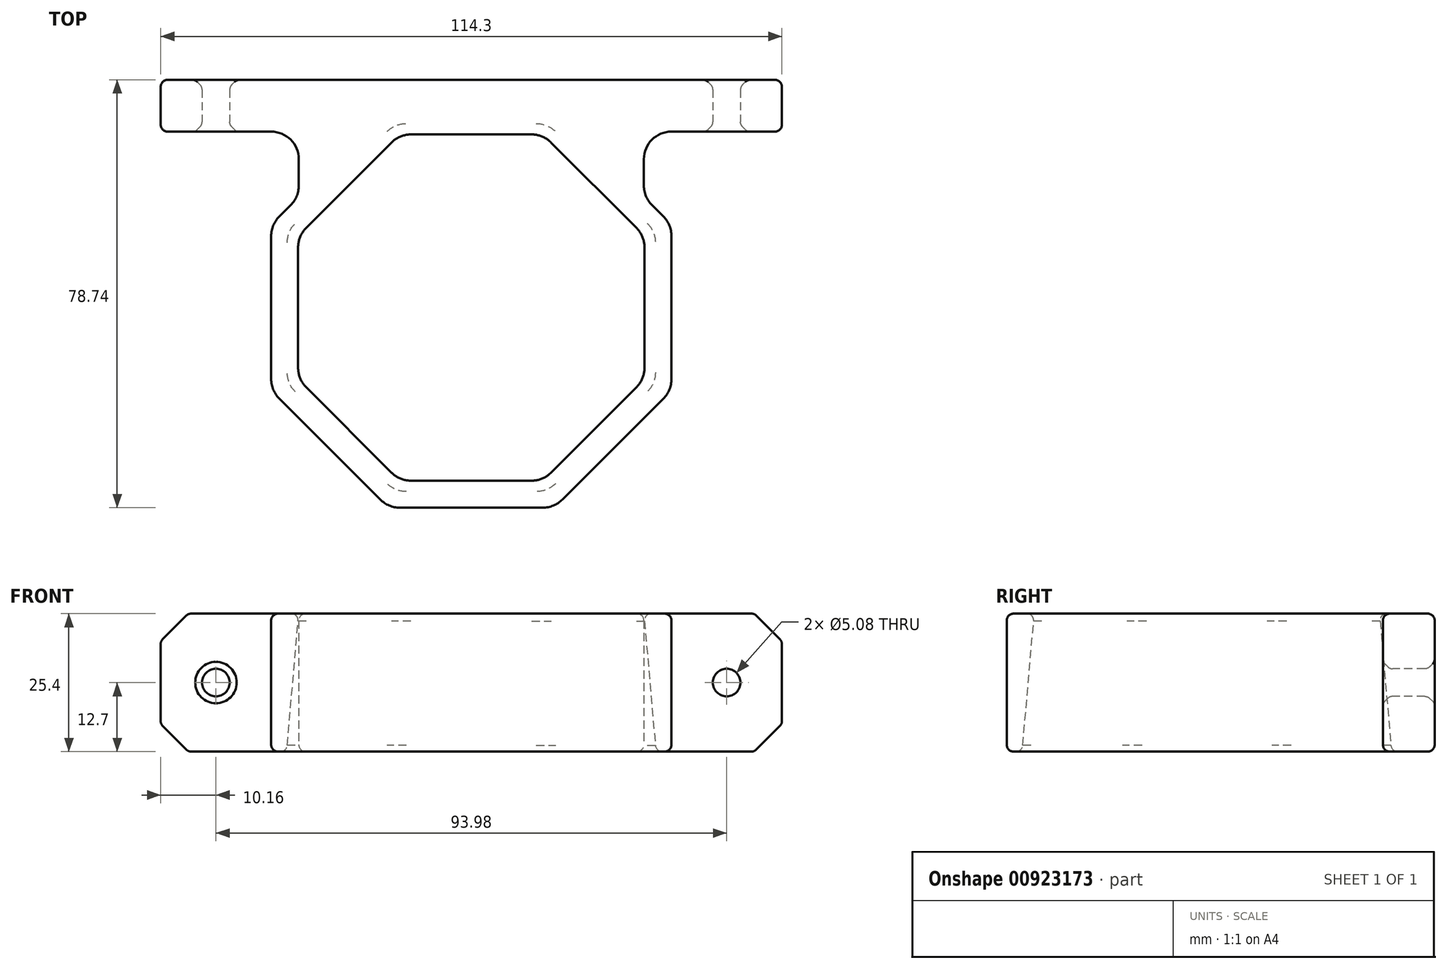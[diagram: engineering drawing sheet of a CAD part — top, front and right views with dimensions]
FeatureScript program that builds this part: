
annotation { "Feature Type Name" : "Feature", "Feature Type Description" : "" }
export const myFeature = defineFeature(function(context is Context, id is Id, definition is map)
    precondition{}
    {
        {
            var Q0;
            Q0=qCreatedBy(makeId("Top.planeOp"),FACE);
            var sketch = newSketch(context, id + "F0", { "sketchPlane" : qUnion([Q0])});
            skCircle(sketch, "E0.cCircle", {"center": v(0, 0) * mm, "radius": 31.75 * mm, "construction": true});
            skLineSegment(sketch, "E0.0", {"start": v(31.75, 13.15) * mm, "end": v(31.75, -13.15) * mm});
            skLineSegment(sketch, "E0.1", {"start": v(31.75, -13.15) * mm, "end": v(13.15, -31.75) * mm});
            skLineSegment(sketch, "E0.2", {"start": v(13.15, -31.75) * mm, "end": v(-13.15, -31.75) * mm});
            skLineSegment(sketch, "E0.3", {"start": v(-13.15, -31.75) * mm, "end": v(-31.75, -13.15) * mm});
            skLineSegment(sketch, "E0.4", {"start": v(-31.75, -13.15) * mm, "end": v(-31.75, 13.15) * mm});
            skLineSegment(sketch, "E0.5", {"start": v(-31.75, 13.15) * mm, "end": v(-13.15, 31.75) * mm});
            skLineSegment(sketch, "E0.6", {"start": v(-13.15, 31.75) * mm, "end": v(13.15, 31.75) * mm});
            skLineSegment(sketch, "E0.7", {"start": v(13.15, 31.75) * mm, "end": v(31.75, 13.15) * mm});
            skPoint(sketch, "E0.0.midPoint", {"position": v(31.75, 0) * mm});
            skLineSegment(sketch, "E1.0", {"start": v(-15.26, 36.83) * mm, "end": v(15.26, 36.83) * mm});
            skLineSegment(sketch, "E1.1", {"start": v(-36.83, 15.26) * mm, "end": v(-15.26, 36.83) * mm});
            skLineSegment(sketch, "E1.2", {"start": v(15.26, 36.83) * mm, "end": v(36.83, 15.26) * mm});
            skLineSegment(sketch, "E1.3", {"start": v(-36.83, -15.26) * mm, "end": v(-36.83, 15.26) * mm});
            skLineSegment(sketch, "E1.4", {"start": v(36.83, 15.26) * mm, "end": v(36.83, -15.26) * mm});
            skLineSegment(sketch, "E1.5", {"start": v(36.83, -15.26) * mm, "end": v(15.26, -36.83) * mm});
            skLineSegment(sketch, "E1.6", {"start": v(15.26, -36.83) * mm, "end": v(-15.26, -36.83) * mm});
            skLineSegment(sketch, "E1.7", {"start": v(-15.26, -36.83) * mm, "end": v(-36.83, -15.26) * mm});
            skLineSegment(sketch, "E2", {"start": v(-31.75, 20.34) * mm, "end": v(-31.75, 41.91) * mm});
            skLineSegment(sketch, "E3", {"start": v(-31.75, 41.91) * mm, "end": v(31.75, 41.91) * mm});
            skLineSegment(sketch, "E4", {"start": v(31.75, 41.91) * mm, "end": v(31.75, 20.34) * mm});
            skLineSegment(sketch, "E5", {"start": v(-31.75, 41.91) * mm, "end": v(-57.15, 41.91) * mm});
            skLineSegment(sketch, "E6", {"start": v(-57.15, 41.91) * mm, "end": v(-57.15, 32.38) * mm});
            skLineSegment(sketch, "E7", {"start": v(-57.15, 32.38) * mm, "end": v(-31.75, 32.38) * mm});
            skLineSegment(sketch, "E8", {"start": v(31.75, 41.91) * mm, "end": v(57.15, 41.91) * mm});
            skLineSegment(sketch, "E9", {"start": v(57.15, 41.91) * mm, "end": v(57.15, 32.39) * mm});
            skLineSegment(sketch, "E10", {"start": v(57.15, 32.39) * mm, "end": v(31.75, 32.39) * mm});
            skSolve(sketch);
        }
        {
            var Q0;
            Q0 = qSketchRegion(id + "F0", true);
            extrude(context, id + "F1", {"entities" : qUnion([Q0]), "depth" : 25.4 * mm, "offsetDistance" : 25.4 * mm});
        }
        {
            var Q0;
            Q0=makeQuery(id+"F1.opExtrude","SWEPT_FACE",FACE,{"disambiguationData":[OSD([sQuery(id+"F0.wireOp",EDGE,"E7")])]});
            var sketch = newSketch(context, id + "F2", { "sketchPlane" : qUnion([Q0])});
            skLineSegment(sketch, "E11", {"start": v(-57.15, 12.7) * mm, "end": v(-46.99, 12.7) * mm, "construction": true});
            skLineSegment(sketch, "E12", {"start": v(47, 12.7) * mm, "end": v(57.15, 12.7) * mm, "construction": true});
            skCircle(sketch, "E13", {"center": v(-46.99, 12.7) * mm, "radius": 2.54 * mm});
            skCircle(sketch, "E14", {"center": v(47, 12.7) * mm, "radius": 2.54 * mm});
            skSolve(sketch);
        }
        {
            var Q0;
            Q0 = qSketchRegion(id + "F2", true);
            extrude(context, id + "F3", {"entities" : qUnion([Q0]), "operationType" : NewBodyOperationType.REMOVE, "endBound" : BoundingType.THROUGH_ALL, "oppositeDirection" : true, "depth" : 25.4 * mm, "offsetDistance" : 25.4 * mm});
        }
        {
            var Q0;
            Q0=makeQuery(id+"F1.opExtrude","CAP_EDGE",EDGE,{"disambiguationData":[OSD([sQuery(id+"F0.wireOp",EDGE,"E0.3")])],"isStart":true});
            var Q1;
            Q1=makeQuery(id+"F1.opExtrude","CAP_EDGE",EDGE,{"disambiguationData":[OSD([sQuery(id+"F0.wireOp",EDGE,"E0.2")])],"isStart":true});
            var Q2;
            Q2=makeQuery(id+"F1.opExtrude","CAP_EDGE",EDGE,{"disambiguationData":[OSD([sQuery(id+"F0.wireOp",EDGE,"E0.1")])],"isStart":true});
            var Q3;
            Q3=makeQuery(id+"F1.opExtrude","CAP_EDGE",EDGE,{"disambiguationData":[OSD([sQuery(id+"F0.wireOp",EDGE,"E0.0")])],"isStart":true});
            var Q4;
            Q4=makeQuery(id+"F1.opExtrude","CAP_EDGE",EDGE,{"disambiguationData":[OSD([sQuery(id+"F0.wireOp",EDGE,"E0.7")])],"isStart":true});
            var Q5;
            Q5=makeQuery(id+"F1.opExtrude","CAP_EDGE",EDGE,{"disambiguationData":[OSD([sQuery(id+"F0.wireOp",EDGE,"E0.6")])],"isStart":true});
            var Q6;
            Q6=makeQuery(id+"F1.opExtrude","CAP_EDGE",EDGE,{"disambiguationData":[OSD([sQuery(id+"F0.wireOp",EDGE,"E0.5")])],"isStart":true});
            var Q7;
            Q7=makeQuery(id+"F1.opExtrude","CAP_EDGE",EDGE,{"disambiguationData":[OSD([sQuery(id+"F0.wireOp",EDGE,"E0.4")])],"isStart":true});
            chamfer(context, id + "F4", {"entities" : qUnion([Q0, Q1, Q2, Q3, Q4, Q5, Q6, Q7]), "chamferType" : ChamferType.OFFSET_ANGLE, "width" : 25.4 * mm, "oppositeDirection" : false, "angle" : 5 * degree, "tangentPropagation" : true});
        }
        {
            var Q0;
            Q0=makeQuery(id+"F1.opExtrude","SWEPT_EDGE",EDGE,{"disambiguationData":[OSD([sQuery(id+"F0.wireOp",EDGE,"E1.6"),sQuery(id+"F0.wireOp",EDGE,"E1.7")])]});
            var Q1;
            Q1=makeQuery(id+"F1.opExtrude","SWEPT_EDGE",EDGE,{"disambiguationData":[OSD([sQuery(id+"F0.wireOp",EDGE,"E1.5"),sQuery(id+"F0.wireOp",EDGE,"E1.6")])]});
            var Q2;
            Q2=makeQuery(id+"F1.opExtrude","SWEPT_EDGE",EDGE,{"disambiguationData":[OSD([sQuery(id+"F0.wireOp",EDGE,"E1.4"),sQuery(id+"F0.wireOp",EDGE,"E1.5")])]});
            var Q3;
            Q3=makeQuery(id+"F1.opExtrude","SWEPT_EDGE",EDGE,{"disambiguationData":[OSD([sQuery(id+"F0.wireOp",EDGE,"E1.2"),sQuery(id+"F0.wireOp",EDGE,"E1.4")])]});
            var Q4;
            Q4=makeQuery(id+"F1.opExtrude","SWEPT_EDGE",EDGE,{"disambiguationData":[OSD([sQuery(id+"F0.wireOp",EDGE,"E1.2"),sQuery(id+"F0.wireOp",EDGE,"E4")])]});
            var Q5;
            Q5=makeQuery(id+"F1.opExtrude","SWEPT_EDGE",EDGE,{"disambiguationData":[OSD([sQuery(id+"F0.wireOp",EDGE,"E4"),sQuery(id+"F0.wireOp",EDGE,"E10")])]});
            var Q6;
            Q6=makeQuery(id+"F1.opExtrude","SWEPT_EDGE",EDGE,{"disambiguationData":[OSD([sQuery(id+"F0.wireOp",EDGE,"E2"),sQuery(id+"F0.wireOp",EDGE,"E7")])]});
            var Q7;
            Q7=makeQuery(id+"F1.opExtrude","SWEPT_EDGE",EDGE,{"disambiguationData":[OSD([sQuery(id+"F0.wireOp",EDGE,"E1.1"),sQuery(id+"F0.wireOp",EDGE,"E2")])]});
            var Q8;
            Q8=makeQuery(id+"F1.opExtrude","SWEPT_EDGE",EDGE,{"disambiguationData":[OSD([sQuery(id+"F0.wireOp",EDGE,"E1.1"),sQuery(id+"F0.wireOp",EDGE,"E1.3")])]});
            var Q9;
            Q9=makeQuery(id+"F1.opExtrude","SWEPT_EDGE",EDGE,{"disambiguationData":[OSD([sQuery(id+"F0.wireOp",EDGE,"E1.3"),sQuery(id+"F0.wireOp",EDGE,"E1.7")])]});
            fillet(context, id + "F5", {"entities" : qUnion([Q0, Q1, Q2, Q3, Q4, Q5, Q6, Q7, Q8, Q9]), "radius" : 5.08 * mm, "tangentPropagation" : true, "allowEdgeOverflow" : false});
        }
        {
            var Q0;
            Q0=makeQuery(id+"F4.opChamfer","BLEND_EDGE",EDGE,{"blendedFrom":[makeQuery(id+"F1.opExtrude","CAP_EDGE",EDGE,{"disambiguationData":[OSD([sQuery(id+"F0.wireOp",EDGE,"E0.5")])],"isStart":true}),makeQuery(id+"F1.opExtrude","CAP_EDGE",EDGE,{"disambiguationData":[OSD([sQuery(id+"F0.wireOp",EDGE,"E0.6")])],"isStart":true})],"blendedInto":[]});
            var Q1;
            Q1=makeQuery(id+"F4.opChamfer","BLEND_EDGE",EDGE,{"blendedFrom":[makeQuery(id+"F1.opExtrude","CAP_EDGE",EDGE,{"disambiguationData":[OSD([sQuery(id+"F0.wireOp",EDGE,"E0.4")])],"isStart":true}),makeQuery(id+"F1.opExtrude","CAP_EDGE",EDGE,{"disambiguationData":[OSD([sQuery(id+"F0.wireOp",EDGE,"E0.5")])],"isStart":true})],"blendedInto":[]});
            var Q2;
            Q2=makeQuery(id+"F4.opChamfer","BLEND_EDGE",EDGE,{"blendedFrom":[makeQuery(id+"F1.opExtrude","CAP_EDGE",EDGE,{"disambiguationData":[OSD([sQuery(id+"F0.wireOp",EDGE,"E0.3")])],"isStart":true}),makeQuery(id+"F1.opExtrude","CAP_EDGE",EDGE,{"disambiguationData":[OSD([sQuery(id+"F0.wireOp",EDGE,"E0.4")])],"isStart":true})],"blendedInto":[]});
            var Q3;
            Q3=makeQuery(id+"F4.opChamfer","BLEND_EDGE",EDGE,{"blendedFrom":[makeQuery(id+"F1.opExtrude","CAP_EDGE",EDGE,{"disambiguationData":[OSD([sQuery(id+"F0.wireOp",EDGE,"E0.2")])],"isStart":true}),makeQuery(id+"F1.opExtrude","CAP_EDGE",EDGE,{"disambiguationData":[OSD([sQuery(id+"F0.wireOp",EDGE,"E0.3")])],"isStart":true})],"blendedInto":[]});
            var Q4;
            Q4=makeQuery(id+"F4.opChamfer","BLEND_EDGE",EDGE,{"blendedFrom":[makeQuery(id+"F1.opExtrude","CAP_EDGE",EDGE,{"disambiguationData":[OSD([sQuery(id+"F0.wireOp",EDGE,"E0.1")])],"isStart":true}),makeQuery(id+"F1.opExtrude","CAP_EDGE",EDGE,{"disambiguationData":[OSD([sQuery(id+"F0.wireOp",EDGE,"E0.2")])],"isStart":true})],"blendedInto":[]});
            var Q5;
            Q5=makeQuery(id+"F4.opChamfer","BLEND_EDGE",EDGE,{"blendedFrom":[makeQuery(id+"F1.opExtrude","CAP_EDGE",EDGE,{"disambiguationData":[OSD([sQuery(id+"F0.wireOp",EDGE,"E0.0")])],"isStart":true}),makeQuery(id+"F1.opExtrude","CAP_EDGE",EDGE,{"disambiguationData":[OSD([sQuery(id+"F0.wireOp",EDGE,"E0.1")])],"isStart":true})],"blendedInto":[]});
            var Q6;
            Q6=makeQuery(id+"F4.opChamfer","BLEND_EDGE",EDGE,{"blendedFrom":[makeQuery(id+"F1.opExtrude","CAP_EDGE",EDGE,{"disambiguationData":[OSD([sQuery(id+"F0.wireOp",EDGE,"E0.0")])],"isStart":true}),makeQuery(id+"F1.opExtrude","CAP_EDGE",EDGE,{"disambiguationData":[OSD([sQuery(id+"F0.wireOp",EDGE,"E0.7")])],"isStart":true})],"blendedInto":[]});
            var Q7;
            Q7=makeQuery(id+"F4.opChamfer","BLEND_EDGE",EDGE,{"blendedFrom":[makeQuery(id+"F1.opExtrude","CAP_EDGE",EDGE,{"disambiguationData":[OSD([sQuery(id+"F0.wireOp",EDGE,"E0.6")])],"isStart":true}),makeQuery(id+"F1.opExtrude","CAP_EDGE",EDGE,{"disambiguationData":[OSD([sQuery(id+"F0.wireOp",EDGE,"E0.7")])],"isStart":true})],"blendedInto":[]});
            fillet(context, id + "F6", {"entities" : qUnion([Q0, Q1, Q2, Q3, Q4, Q5, Q6, Q7]), "radius" : 5.08 * mm, "tangentPropagation" : true, "allowEdgeOverflow" : false});
        }
        {
            var Q0;
            Q0=makeQuery(id+"F1.opExtrude","CAP_EDGE",EDGE,{"disambiguationData":[OSD([sQuery(id+"F0.wireOp",EDGE,"E9")])],"isStart":false});
            var Q1;
            Q1=makeQuery(id+"F1.opExtrude","CAP_EDGE",EDGE,{"disambiguationData":[OSD([sQuery(id+"F0.wireOp",EDGE,"E6")])],"isStart":false});
            var Q2;
            Q2=makeQuery(id+"F1.opExtrude","CAP_EDGE",EDGE,{"disambiguationData":[OSD([sQuery(id+"F0.wireOp",EDGE,"E6")])],"isStart":true});
            var Q3;
            Q3=makeQuery(id+"F1.opExtrude","CAP_EDGE",EDGE,{"disambiguationData":[OSD([sQuery(id+"F0.wireOp",EDGE,"E9")])],"isStart":true});
            chamfer(context, id + "F7", {"entities" : qUnion([Q0, Q1, Q2, Q3]), "width" : 5.08 * mm, "tangentPropagation" : true});
        }
        {
            var Q0;
            {var subQ0=sQuery(id+"F0.wireOp",EDGE,"E6");Q0=makeQuery(id+"F7.opChamfer","BLEND_EDGE",EDGE,{"blendedFrom":[makeQuery(id+"F1.opExtrude","CAP_EDGE",EDGE,{"disambiguationData":[OSD([subQ0])],"isStart":false}),makeQuery(id+"F1.opExtrude","CAP_FACE",FACE,{"disambiguationData":[OSD([sQuery(id+"F0.wireOp",EDGE,"E0.0"),sQuery(id+"F0.wireOp",EDGE,"E0.1"),sQuery(id+"F0.wireOp",EDGE,"E0.2"),sQuery(id+"F0.wireOp",EDGE,"E0.3"),sQuery(id+"F0.wireOp",EDGE,"E0.4"),sQuery(id+"F0.wireOp",EDGE,"E0.5"),sQuery(id+"F0.wireOp",EDGE,"E0.6"),sQuery(id+"F0.wireOp",EDGE,"E0.7"),sQuery(id+"F0.wireOp",EDGE,"E1.1"),sQuery(id+"F0.wireOp",EDGE,"E1.2"),sQuery(id+"F0.wireOp",EDGE,"E1.3"),sQuery(id+"F0.wireOp",EDGE,"E1.4"),sQuery(id+"F0.wireOp",EDGE,"E1.5"),sQuery(id+"F0.wireOp",EDGE,"E1.6"),sQuery(id+"F0.wireOp",EDGE,"E1.7"),sQuery(id+"F0.wireOp",EDGE,"E2"),sQuery(id+"F0.wireOp",EDGE,"E3"),sQuery(id+"F0.wireOp",EDGE,"E4"),sQuery(id+"F0.wireOp",EDGE,"E5"),subQ0,sQuery(id+"F0.wireOp",EDGE,"E7"),sQuery(id+"F0.wireOp",EDGE,"E8"),sQuery(id+"F0.wireOp",EDGE,"E9"),sQuery(id+"F0.wireOp",EDGE,"E10")])],"isStart":false})],"blendedInto":[makeQuery(id+"F1.opExtrude","CAP_FACE",FACE,{"disambiguationData":[OSD([sQuery(id+"F0.wireOp",EDGE,"E0.0"),sQuery(id+"F0.wireOp",EDGE,"E0.1"),sQuery(id+"F0.wireOp",EDGE,"E0.2"),sQuery(id+"F0.wireOp",EDGE,"E0.3"),sQuery(id+"F0.wireOp",EDGE,"E0.4"),sQuery(id+"F0.wireOp",EDGE,"E0.5"),sQuery(id+"F0.wireOp",EDGE,"E0.6"),sQuery(id+"F0.wireOp",EDGE,"E0.7"),sQuery(id+"F0.wireOp",EDGE,"E1.1"),sQuery(id+"F0.wireOp",EDGE,"E1.2"),sQuery(id+"F0.wireOp",EDGE,"E1.3"),sQuery(id+"F0.wireOp",EDGE,"E1.4"),sQuery(id+"F0.wireOp",EDGE,"E1.5"),sQuery(id+"F0.wireOp",EDGE,"E1.6"),sQuery(id+"F0.wireOp",EDGE,"E1.7"),sQuery(id+"F0.wireOp",EDGE,"E2"),sQuery(id+"F0.wireOp",EDGE,"E3"),sQuery(id+"F0.wireOp",EDGE,"E4"),sQuery(id+"F0.wireOp",EDGE,"E5"),subQ0,sQuery(id+"F0.wireOp",EDGE,"E7"),sQuery(id+"F0.wireOp",EDGE,"E8"),sQuery(id+"F0.wireOp",EDGE,"E9"),sQuery(id+"F0.wireOp",EDGE,"E10")])],"isStart":false})]});}
            var Q1;
            {var subQ0=sQuery(id+"F0.wireOp",EDGE,"E6");Q1=makeQuery(id+"F7.opChamfer","BLEND_EDGE",EDGE,{"blendedFrom":[makeQuery(id+"F1.opExtrude","CAP_EDGE",EDGE,{"disambiguationData":[OSD([subQ0])],"isStart":false}),makeQuery(id+"F1.opExtrude","SWEPT_FACE",FACE,{"disambiguationData":[OSD([subQ0])]})],"blendedInto":[makeQuery(id+"F1.opExtrude","SWEPT_FACE",FACE,{"disambiguationData":[OSD([subQ0])]})]});}
            var Q2;
            {var subQ0=sQuery(id+"F0.wireOp",EDGE,"E6");Q2=makeQuery(id+"F7.opChamfer","BLEND_EDGE",EDGE,{"blendedFrom":[makeQuery(id+"F1.opExtrude","CAP_EDGE",EDGE,{"disambiguationData":[OSD([subQ0])],"isStart":true}),makeQuery(id+"F1.opExtrude","SWEPT_FACE",FACE,{"disambiguationData":[OSD([subQ0])]})],"blendedInto":[makeQuery(id+"F1.opExtrude","SWEPT_FACE",FACE,{"disambiguationData":[OSD([subQ0])]})]});}
            var Q3;
            {var subQ0=sQuery(id+"F0.wireOp",EDGE,"E6");Q3=makeQuery(id+"F7.opChamfer","BLEND_EDGE",EDGE,{"blendedFrom":[makeQuery(id+"F1.opExtrude","CAP_EDGE",EDGE,{"disambiguationData":[OSD([subQ0])],"isStart":true}),makeQuery(id+"F1.opExtrude","CAP_FACE",FACE,{"disambiguationData":[OSD([sQuery(id+"F0.wireOp",EDGE,"E0.0"),sQuery(id+"F0.wireOp",EDGE,"E0.1"),sQuery(id+"F0.wireOp",EDGE,"E0.2"),sQuery(id+"F0.wireOp",EDGE,"E0.3"),sQuery(id+"F0.wireOp",EDGE,"E0.4"),sQuery(id+"F0.wireOp",EDGE,"E0.5"),sQuery(id+"F0.wireOp",EDGE,"E0.6"),sQuery(id+"F0.wireOp",EDGE,"E0.7"),sQuery(id+"F0.wireOp",EDGE,"E1.1"),sQuery(id+"F0.wireOp",EDGE,"E1.2"),sQuery(id+"F0.wireOp",EDGE,"E1.3"),sQuery(id+"F0.wireOp",EDGE,"E1.4"),sQuery(id+"F0.wireOp",EDGE,"E1.5"),sQuery(id+"F0.wireOp",EDGE,"E1.6"),sQuery(id+"F0.wireOp",EDGE,"E1.7"),sQuery(id+"F0.wireOp",EDGE,"E2"),sQuery(id+"F0.wireOp",EDGE,"E3"),sQuery(id+"F0.wireOp",EDGE,"E4"),sQuery(id+"F0.wireOp",EDGE,"E5"),subQ0,sQuery(id+"F0.wireOp",EDGE,"E7"),sQuery(id+"F0.wireOp",EDGE,"E8"),sQuery(id+"F0.wireOp",EDGE,"E9"),sQuery(id+"F0.wireOp",EDGE,"E10")])],"isStart":true})],"blendedInto":[makeQuery(id+"F1.opExtrude","CAP_FACE",FACE,{"disambiguationData":[OSD([sQuery(id+"F0.wireOp",EDGE,"E0.0"),sQuery(id+"F0.wireOp",EDGE,"E0.1"),sQuery(id+"F0.wireOp",EDGE,"E0.2"),sQuery(id+"F0.wireOp",EDGE,"E0.3"),sQuery(id+"F0.wireOp",EDGE,"E0.4"),sQuery(id+"F0.wireOp",EDGE,"E0.5"),sQuery(id+"F0.wireOp",EDGE,"E0.6"),sQuery(id+"F0.wireOp",EDGE,"E0.7"),sQuery(id+"F0.wireOp",EDGE,"E1.1"),sQuery(id+"F0.wireOp",EDGE,"E1.2"),sQuery(id+"F0.wireOp",EDGE,"E1.3"),sQuery(id+"F0.wireOp",EDGE,"E1.4"),sQuery(id+"F0.wireOp",EDGE,"E1.5"),sQuery(id+"F0.wireOp",EDGE,"E1.6"),sQuery(id+"F0.wireOp",EDGE,"E1.7"),sQuery(id+"F0.wireOp",EDGE,"E2"),sQuery(id+"F0.wireOp",EDGE,"E3"),sQuery(id+"F0.wireOp",EDGE,"E4"),sQuery(id+"F0.wireOp",EDGE,"E5"),subQ0,sQuery(id+"F0.wireOp",EDGE,"E7"),sQuery(id+"F0.wireOp",EDGE,"E8"),sQuery(id+"F0.wireOp",EDGE,"E9"),sQuery(id+"F0.wireOp",EDGE,"E10")])],"isStart":true})]});}
            var Q4;
            {var subQ0=sQuery(id+"F0.wireOp",EDGE,"E9");Q4=makeQuery(id+"F7.opChamfer","BLEND_EDGE",EDGE,{"blendedFrom":[makeQuery(id+"F1.opExtrude","CAP_EDGE",EDGE,{"disambiguationData":[OSD([subQ0])],"isStart":true}),makeQuery(id+"F1.opExtrude","CAP_FACE",FACE,{"disambiguationData":[OSD([sQuery(id+"F0.wireOp",EDGE,"E0.0"),sQuery(id+"F0.wireOp",EDGE,"E0.1"),sQuery(id+"F0.wireOp",EDGE,"E0.2"),sQuery(id+"F0.wireOp",EDGE,"E0.3"),sQuery(id+"F0.wireOp",EDGE,"E0.4"),sQuery(id+"F0.wireOp",EDGE,"E0.5"),sQuery(id+"F0.wireOp",EDGE,"E0.6"),sQuery(id+"F0.wireOp",EDGE,"E0.7"),sQuery(id+"F0.wireOp",EDGE,"E1.1"),sQuery(id+"F0.wireOp",EDGE,"E1.2"),sQuery(id+"F0.wireOp",EDGE,"E1.3"),sQuery(id+"F0.wireOp",EDGE,"E1.4"),sQuery(id+"F0.wireOp",EDGE,"E1.5"),sQuery(id+"F0.wireOp",EDGE,"E1.6"),sQuery(id+"F0.wireOp",EDGE,"E1.7"),sQuery(id+"F0.wireOp",EDGE,"E2"),sQuery(id+"F0.wireOp",EDGE,"E3"),sQuery(id+"F0.wireOp",EDGE,"E4"),sQuery(id+"F0.wireOp",EDGE,"E5"),sQuery(id+"F0.wireOp",EDGE,"E6"),sQuery(id+"F0.wireOp",EDGE,"E7"),sQuery(id+"F0.wireOp",EDGE,"E8"),subQ0,sQuery(id+"F0.wireOp",EDGE,"E10")])],"isStart":true})],"blendedInto":[makeQuery(id+"F1.opExtrude","CAP_FACE",FACE,{"disambiguationData":[OSD([sQuery(id+"F0.wireOp",EDGE,"E0.0"),sQuery(id+"F0.wireOp",EDGE,"E0.1"),sQuery(id+"F0.wireOp",EDGE,"E0.2"),sQuery(id+"F0.wireOp",EDGE,"E0.3"),sQuery(id+"F0.wireOp",EDGE,"E0.4"),sQuery(id+"F0.wireOp",EDGE,"E0.5"),sQuery(id+"F0.wireOp",EDGE,"E0.6"),sQuery(id+"F0.wireOp",EDGE,"E0.7"),sQuery(id+"F0.wireOp",EDGE,"E1.1"),sQuery(id+"F0.wireOp",EDGE,"E1.2"),sQuery(id+"F0.wireOp",EDGE,"E1.3"),sQuery(id+"F0.wireOp",EDGE,"E1.4"),sQuery(id+"F0.wireOp",EDGE,"E1.5"),sQuery(id+"F0.wireOp",EDGE,"E1.6"),sQuery(id+"F0.wireOp",EDGE,"E1.7"),sQuery(id+"F0.wireOp",EDGE,"E2"),sQuery(id+"F0.wireOp",EDGE,"E3"),sQuery(id+"F0.wireOp",EDGE,"E4"),sQuery(id+"F0.wireOp",EDGE,"E5"),sQuery(id+"F0.wireOp",EDGE,"E6"),sQuery(id+"F0.wireOp",EDGE,"E7"),sQuery(id+"F0.wireOp",EDGE,"E8"),subQ0,sQuery(id+"F0.wireOp",EDGE,"E10")])],"isStart":true})]});}
            var Q5;
            {var subQ0=sQuery(id+"F0.wireOp",EDGE,"E9");Q5=makeQuery(id+"F7.opChamfer","BLEND_EDGE",EDGE,{"blendedFrom":[makeQuery(id+"F1.opExtrude","CAP_EDGE",EDGE,{"disambiguationData":[OSD([subQ0])],"isStart":true}),makeQuery(id+"F1.opExtrude","SWEPT_FACE",FACE,{"disambiguationData":[OSD([subQ0])]})],"blendedInto":[makeQuery(id+"F1.opExtrude","SWEPT_FACE",FACE,{"disambiguationData":[OSD([subQ0])]})]});}
            var Q6;
            {var subQ0=sQuery(id+"F0.wireOp",EDGE,"E9");Q6=makeQuery(id+"F7.opChamfer","BLEND_EDGE",EDGE,{"blendedFrom":[makeQuery(id+"F1.opExtrude","CAP_EDGE",EDGE,{"disambiguationData":[OSD([subQ0])],"isStart":false}),makeQuery(id+"F1.opExtrude","SWEPT_FACE",FACE,{"disambiguationData":[OSD([subQ0])]})],"blendedInto":[makeQuery(id+"F1.opExtrude","SWEPT_FACE",FACE,{"disambiguationData":[OSD([subQ0])]})]});}
            var Q7;
            {var subQ0=sQuery(id+"F0.wireOp",EDGE,"E9");Q7=makeQuery(id+"F7.opChamfer","BLEND_EDGE",EDGE,{"blendedFrom":[makeQuery(id+"F1.opExtrude","CAP_EDGE",EDGE,{"disambiguationData":[OSD([subQ0])],"isStart":false}),makeQuery(id+"F1.opExtrude","CAP_FACE",FACE,{"disambiguationData":[OSD([sQuery(id+"F0.wireOp",EDGE,"E0.0"),sQuery(id+"F0.wireOp",EDGE,"E0.1"),sQuery(id+"F0.wireOp",EDGE,"E0.2"),sQuery(id+"F0.wireOp",EDGE,"E0.3"),sQuery(id+"F0.wireOp",EDGE,"E0.4"),sQuery(id+"F0.wireOp",EDGE,"E0.5"),sQuery(id+"F0.wireOp",EDGE,"E0.6"),sQuery(id+"F0.wireOp",EDGE,"E0.7"),sQuery(id+"F0.wireOp",EDGE,"E1.1"),sQuery(id+"F0.wireOp",EDGE,"E1.2"),sQuery(id+"F0.wireOp",EDGE,"E1.3"),sQuery(id+"F0.wireOp",EDGE,"E1.4"),sQuery(id+"F0.wireOp",EDGE,"E1.5"),sQuery(id+"F0.wireOp",EDGE,"E1.6"),sQuery(id+"F0.wireOp",EDGE,"E1.7"),sQuery(id+"F0.wireOp",EDGE,"E2"),sQuery(id+"F0.wireOp",EDGE,"E3"),sQuery(id+"F0.wireOp",EDGE,"E4"),sQuery(id+"F0.wireOp",EDGE,"E5"),sQuery(id+"F0.wireOp",EDGE,"E6"),sQuery(id+"F0.wireOp",EDGE,"E7"),sQuery(id+"F0.wireOp",EDGE,"E8"),subQ0,sQuery(id+"F0.wireOp",EDGE,"E10")])],"isStart":false})],"blendedInto":[makeQuery(id+"F1.opExtrude","CAP_FACE",FACE,{"disambiguationData":[OSD([sQuery(id+"F0.wireOp",EDGE,"E0.0"),sQuery(id+"F0.wireOp",EDGE,"E0.1"),sQuery(id+"F0.wireOp",EDGE,"E0.2"),sQuery(id+"F0.wireOp",EDGE,"E0.3"),sQuery(id+"F0.wireOp",EDGE,"E0.4"),sQuery(id+"F0.wireOp",EDGE,"E0.5"),sQuery(id+"F0.wireOp",EDGE,"E0.6"),sQuery(id+"F0.wireOp",EDGE,"E0.7"),sQuery(id+"F0.wireOp",EDGE,"E1.1"),sQuery(id+"F0.wireOp",EDGE,"E1.2"),sQuery(id+"F0.wireOp",EDGE,"E1.3"),sQuery(id+"F0.wireOp",EDGE,"E1.4"),sQuery(id+"F0.wireOp",EDGE,"E1.5"),sQuery(id+"F0.wireOp",EDGE,"E1.6"),sQuery(id+"F0.wireOp",EDGE,"E1.7"),sQuery(id+"F0.wireOp",EDGE,"E2"),sQuery(id+"F0.wireOp",EDGE,"E3"),sQuery(id+"F0.wireOp",EDGE,"E4"),sQuery(id+"F0.wireOp",EDGE,"E5"),sQuery(id+"F0.wireOp",EDGE,"E6"),sQuery(id+"F0.wireOp",EDGE,"E7"),sQuery(id+"F0.wireOp",EDGE,"E8"),subQ0,sQuery(id+"F0.wireOp",EDGE,"E10")])],"isStart":false})]});}
            fillet(context, id + "F8", {"entities" : qUnion([Q0, Q1, Q2, Q3, Q4, Q5, Q6, Q7]), "radius" : 1.27 * mm, "tangentPropagation" : true, "allowEdgeOverflow" : false});
        }
        {
            var Q0;
            Q0=makeQuery(id+"F1.opExtrude","CAP_FACE",FACE,{"disambiguationData":[OSD([sQuery(id+"F0.wireOp",EDGE,"E0.0"),sQuery(id+"F0.wireOp",EDGE,"E0.1"),sQuery(id+"F0.wireOp",EDGE,"E0.2"),sQuery(id+"F0.wireOp",EDGE,"E0.3"),sQuery(id+"F0.wireOp",EDGE,"E0.4"),sQuery(id+"F0.wireOp",EDGE,"E0.5"),sQuery(id+"F0.wireOp",EDGE,"E0.6"),sQuery(id+"F0.wireOp",EDGE,"E0.7"),sQuery(id+"F0.wireOp",EDGE,"E1.1"),sQuery(id+"F0.wireOp",EDGE,"E1.2"),sQuery(id+"F0.wireOp",EDGE,"E1.3"),sQuery(id+"F0.wireOp",EDGE,"E1.4"),sQuery(id+"F0.wireOp",EDGE,"E1.5"),sQuery(id+"F0.wireOp",EDGE,"E1.6"),sQuery(id+"F0.wireOp",EDGE,"E1.7"),sQuery(id+"F0.wireOp",EDGE,"E2"),sQuery(id+"F0.wireOp",EDGE,"E3"),sQuery(id+"F0.wireOp",EDGE,"E4"),sQuery(id+"F0.wireOp",EDGE,"E5"),sQuery(id+"F0.wireOp",EDGE,"E6"),sQuery(id+"F0.wireOp",EDGE,"E7"),sQuery(id+"F0.wireOp",EDGE,"E8"),sQuery(id+"F0.wireOp",EDGE,"E9"),sQuery(id+"F0.wireOp",EDGE,"E10")])],"isStart":false});
            var Q1;
            {var subQ0=sQuery(id+"F0.wireOp",EDGE,"E0.5");Q1=makeQuery(id+"F4.opChamfer","BLEND_EDGE",EDGE,{"blendedFrom":[makeQuery(id+"F1.opExtrude","CAP_EDGE",EDGE,{"disambiguationData":[OSD([subQ0])],"isStart":true}),makeQuery(id+"F1.opExtrude","CAP_FACE",FACE,{"disambiguationData":[OSD([sQuery(id+"F0.wireOp",EDGE,"E0.0"),sQuery(id+"F0.wireOp",EDGE,"E0.1"),sQuery(id+"F0.wireOp",EDGE,"E0.2"),sQuery(id+"F0.wireOp",EDGE,"E0.3"),sQuery(id+"F0.wireOp",EDGE,"E0.4"),subQ0,sQuery(id+"F0.wireOp",EDGE,"E0.6"),sQuery(id+"F0.wireOp",EDGE,"E0.7"),sQuery(id+"F0.wireOp",EDGE,"E1.1"),sQuery(id+"F0.wireOp",EDGE,"E1.2"),sQuery(id+"F0.wireOp",EDGE,"E1.3"),sQuery(id+"F0.wireOp",EDGE,"E1.4"),sQuery(id+"F0.wireOp",EDGE,"E1.5"),sQuery(id+"F0.wireOp",EDGE,"E1.6"),sQuery(id+"F0.wireOp",EDGE,"E1.7"),sQuery(id+"F0.wireOp",EDGE,"E2"),sQuery(id+"F0.wireOp",EDGE,"E3"),sQuery(id+"F0.wireOp",EDGE,"E4"),sQuery(id+"F0.wireOp",EDGE,"E5"),sQuery(id+"F0.wireOp",EDGE,"E6"),sQuery(id+"F0.wireOp",EDGE,"E7"),sQuery(id+"F0.wireOp",EDGE,"E8"),sQuery(id+"F0.wireOp",EDGE,"E9"),sQuery(id+"F0.wireOp",EDGE,"E10")])],"isStart":true})],"blendedInto":[makeQuery(id+"F1.opExtrude","CAP_FACE",FACE,{"disambiguationData":[OSD([sQuery(id+"F0.wireOp",EDGE,"E0.0"),sQuery(id+"F0.wireOp",EDGE,"E0.1"),sQuery(id+"F0.wireOp",EDGE,"E0.2"),sQuery(id+"F0.wireOp",EDGE,"E0.3"),sQuery(id+"F0.wireOp",EDGE,"E0.4"),subQ0,sQuery(id+"F0.wireOp",EDGE,"E0.6"),sQuery(id+"F0.wireOp",EDGE,"E0.7"),sQuery(id+"F0.wireOp",EDGE,"E1.1"),sQuery(id+"F0.wireOp",EDGE,"E1.2"),sQuery(id+"F0.wireOp",EDGE,"E1.3"),sQuery(id+"F0.wireOp",EDGE,"E1.4"),sQuery(id+"F0.wireOp",EDGE,"E1.5"),sQuery(id+"F0.wireOp",EDGE,"E1.6"),sQuery(id+"F0.wireOp",EDGE,"E1.7"),sQuery(id+"F0.wireOp",EDGE,"E2"),sQuery(id+"F0.wireOp",EDGE,"E3"),sQuery(id+"F0.wireOp",EDGE,"E4"),sQuery(id+"F0.wireOp",EDGE,"E5"),sQuery(id+"F0.wireOp",EDGE,"E6"),sQuery(id+"F0.wireOp",EDGE,"E7"),sQuery(id+"F0.wireOp",EDGE,"E8"),sQuery(id+"F0.wireOp",EDGE,"E9"),sQuery(id+"F0.wireOp",EDGE,"E10")])],"isStart":true})]});}
            fillet(context, id + "F9", {"entities" : qUnion([Q0, Q1]), "radius" : 1.27 * mm, "tangentPropagation" : true, "allowEdgeOverflow" : false});
        }
        {
            var Q0;
            Q0=makeQuery(id+"F3.boolean.opBoolean","COPY",FACE,{"derivedFrom":makeQuery(id+"F3.opExtrude","SWEPT_FACE",FACE,{"disambiguationData":[OSD([sQuery(id+"F2.wireOp",EDGE,"E14")])]})});
            var Q1;
            Q1=makeQuery(id+"F3.boolean.opBoolean","COPY",FACE,{"derivedFrom":makeQuery(id+"F3.opExtrude","SWEPT_FACE",FACE,{"disambiguationData":[OSD([sQuery(id+"F2.wireOp",EDGE,"E13")])]})});
            chamfer(context, id + "F10", {"entities" : qUnion([Q0, Q1]), "width" : 1.27 * mm, "tangentPropagation" : true});
        }
        {
            var Q0;
            Q0=makeQuery(id+"F3.boolean.opBoolean","COPY",FACE,{"derivedFrom":makeQuery(id+"F3.opExtrude","SWEPT_FACE",FACE,{"disambiguationData":[OSD([sQuery(id+"F2.wireOp",EDGE,"E13")])]})});
            var Q1;
            Q1=makeQuery(id+"F3.boolean.opBoolean","COPY",FACE,{"derivedFrom":makeQuery(id+"F3.opExtrude","SWEPT_FACE",FACE,{"disambiguationData":[OSD([sQuery(id+"F2.wireOp",EDGE,"E14")])]})});
            var Q2;
            {var subQ0=makeQuery(id+"F1.opExtrude","SWEPT_FACE",FACE,{"disambiguationData":[OSD([sQuery(id+"F0.wireOp",EDGE,"E3"),sQuery(id+"F0.wireOp",EDGE,"E5"),sQuery(id+"F0.wireOp",EDGE,"E8")])]});Q2=makeQuery(id+"F10.opChamfer","BLEND_EDGE",EDGE,{"blendedFrom":[makeQuery(id+"F3.boolean.opBoolean","INTERSECT",EDGE,{"derivedFrom":[subQ0,makeQuery(id+"F3.opExtrude","SWEPT_FACE",FACE,{"disambiguationData":[OSD([sQuery(id+"F2.wireOp",EDGE,"E14")])]})]}),subQ0],"blendedInto":[subQ0]});}
            var Q3;
            {var subQ0=makeQuery(id+"F1.opExtrude","SWEPT_FACE",FACE,{"disambiguationData":[OSD([sQuery(id+"F0.wireOp",EDGE,"E3"),sQuery(id+"F0.wireOp",EDGE,"E5"),sQuery(id+"F0.wireOp",EDGE,"E8")])]});Q3=makeQuery(id+"F10.opChamfer","BLEND_EDGE",EDGE,{"blendedFrom":[makeQuery(id+"F3.boolean.opBoolean","INTERSECT",EDGE,{"derivedFrom":[subQ0,makeQuery(id+"F3.opExtrude","SWEPT_FACE",FACE,{"disambiguationData":[OSD([sQuery(id+"F2.wireOp",EDGE,"E13")])]})]}),subQ0],"blendedInto":[subQ0]});}
            var Q4;
            Q4=makeQuery(id+"F10.opChamfer","BLEND_EDGE",EDGE,{"blendedFrom":[makeQuery(id+"F3.boolean.opBoolean","COPY",EDGE,{"derivedFrom":makeQuery(id+"F3.opExtrude","CAP_EDGE",EDGE,{"disambiguationData":[OSD([sQuery(id+"F2.wireOp",EDGE,"E13")])],"isStart":true})}),makeQuery(id+"F1.opExtrude","SWEPT_FACE",FACE,{"disambiguationData":[OSD([sQuery(id+"F0.wireOp",EDGE,"E7")])]})],"blendedInto":[makeQuery(id+"F1.opExtrude","SWEPT_FACE",FACE,{"disambiguationData":[OSD([sQuery(id+"F0.wireOp",EDGE,"E7")])]})]});
            var Q5;
            Q5=makeQuery(id+"F1.opExtrude","SWEPT_FACE",FACE,{"disambiguationData":[OSD([sQuery(id+"F0.wireOp",EDGE,"E10")])]});
            fillet(context, id + "F11", {"entities" : qUnion([Q0, Q1, Q2, Q3, Q4, Q5]), "radius" : 1.27 * mm, "tangentPropagation" : true, "allowEdgeOverflow" : false});
        }
    });
